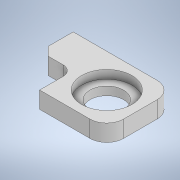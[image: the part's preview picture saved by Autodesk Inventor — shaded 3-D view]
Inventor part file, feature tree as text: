
AUTODESK INVENTOR PART (.ipt)
format: ipt  version: 2021 (Build 250183000, 183)  size: 130,560 bytes
history: native  units: mm
features: fillet x2, sketch x2, other x1, extrude x1, hole x1, chamfer x1
ambient origin geometry x8: Origin, YZ Plane, XZ Plane, XY Plane, X Axis, Y Axis, Z Axis, Center Point
bodies: Body1 (feature_tree)
feature tree (8):
  other  "Sólido1"
  extrude  "Extrusão1"  Depth=300.0mm
  hole  "Furo1"  [1 undecoded]
  fillet  "Arredondamento1"  Radius=50.0mm
  fillet  "Arredondamento2"  Radius=100.0mm
  chamfer  "Chanfro1"  Distance=100.0mm
  sketch  "Esboço1"  dims[d0=200.0mm d1=300.0mm]
  sketch  "Esboço2"  dims[d3=200.0mm d4=100.0mm d5=50.0mm d6=0.0mm d7=100.0mm d8=100.0mm d9=6.0mm d10=150.0mm d11=25.0mm d12=90.0deg d13=8.0mm d14=20.594885mm d15=100.0mm d16=50.0mm d17=30.0mm d18=25.0mm d19=2.0mm d20=45.0deg]
note: 1 required parameter value undecoded (feature->parameter linkage not recoverable at this tier; creation-order binding heuristic only, values carry confidence <= 0.55)
